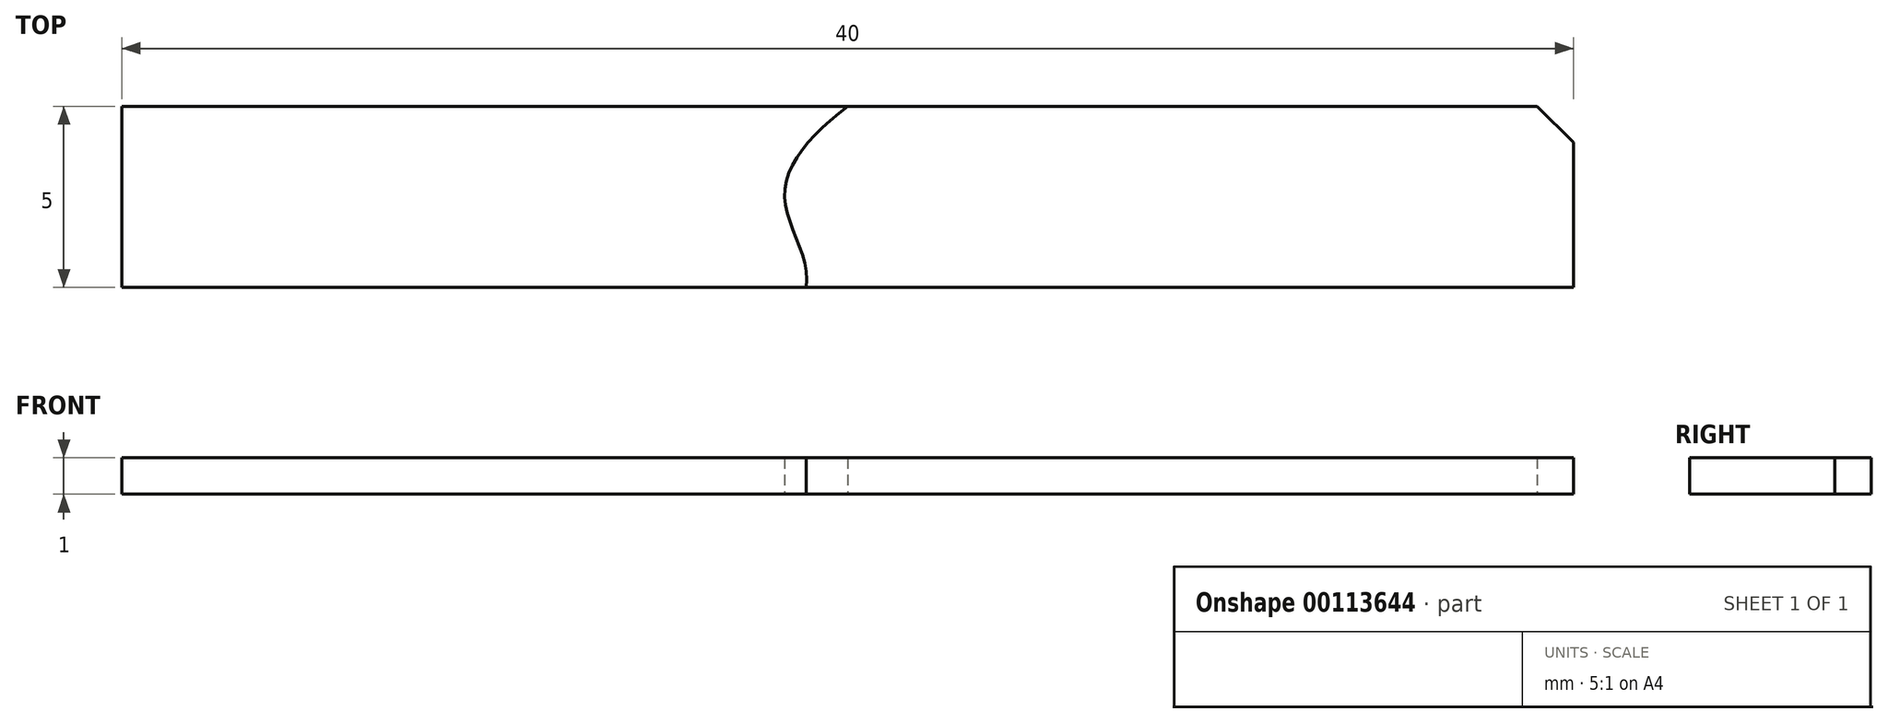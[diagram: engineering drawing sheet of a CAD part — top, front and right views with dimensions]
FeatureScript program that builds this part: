
annotation { "Feature Type Name" : "Feature", "Feature Type Description" : "" }
export const myFeature = defineFeature(function(context is Context, id is Id, definition is map)
    precondition{}
    {
        {
            var Q0;
            Q0=qCreatedBy(makeId("Top.planeOp"),FACE);
            var sketch = newSketch(context, id + "F0", { "sketchPlane" : qUnion([Q0])});
            skLineSegment(sketch, "E0.bottom", {"start": v(20, -2.5) * mm, "end": v(-20, -2.5) * mm});
            skLineSegment(sketch, "E0.top", {"start": v(20, 2.5) * mm, "end": v(-20, 2.5) * mm});
            skLineSegment(sketch, "E0.left", {"start": v(20, -2.5) * mm, "end": v(20, 2.5) * mm});
            skLineSegment(sketch, "E0.right", {"start": v(-20, -2.5) * mm, "end": v(-20, 2.5) * mm});
            skPoint(sketch, "E0.middle", {"position": v(0, 0) * mm});
            skPoint(sketch, "E1", {"position": v(0, 2.5) * mm});
            skPoint(sketch, "E2", {"position": v(-1.74, 0) * mm});
            skPoint(sketch, "E3", {"position": v(-1.15, -2.5) * mm});
            skFitSpline(sketch, "E4", {"points": [v(0, 2.5) * mm, v(-1.74, 0) * mm, v(-1.15, -2.5) * mm], "startDerivative": vector(-5.76, -4.45) * mm, "endDerivative": vector(-0.93, -5.14) * mm});
            skSolve(sketch);
        }
        {
            var Q0;
            {var subQ0=sQuery(id+"F0.wireOp",EDGE,"E0.right");Q0=makeQuery(id+"F0.imprint","IMPRINT",FACE,{"disambiguationData":[TD([[makeQuery(id+"F0.imprint","IMPRINT",EDGE,{"derivedFrom":subQ0}),-1.0]])]});}
            extrude(context, id + "F1", {"entities" : qUnion([Q0]), "depth" : 1 * mm});
        }
        {
            var Q0;
            {var subQ0=sQuery(id+"F0.wireOp",EDGE,"E0.left");Q0=makeQuery(id+"F0.imprint","IMPRINT",FACE,{"disambiguationData":[TD([[makeQuery(id+"F0.imprint","IMPRINT",EDGE,{"derivedFrom":subQ0}),1.0]])]});}
            extrude(context, id + "F2", {"entities" : qUnion([Q0]), "depth" : 1 * mm});
        }
        {
            var Q0;
            Q0=makeQuery(id+"F2.opExtrude","SWEPT_EDGE",EDGE,{"disambiguationData":[OSD([sQuery(id+"F0.wireOp",EDGE,"E0.top"),sQuery(id+"F0.wireOp",EDGE,"E0.left")])]});
            chamfer(context, id + "F3", {"entities" : qUnion([Q0]), "width" : 1 * mm, "tangentPropagation" : true});
        }
    });
